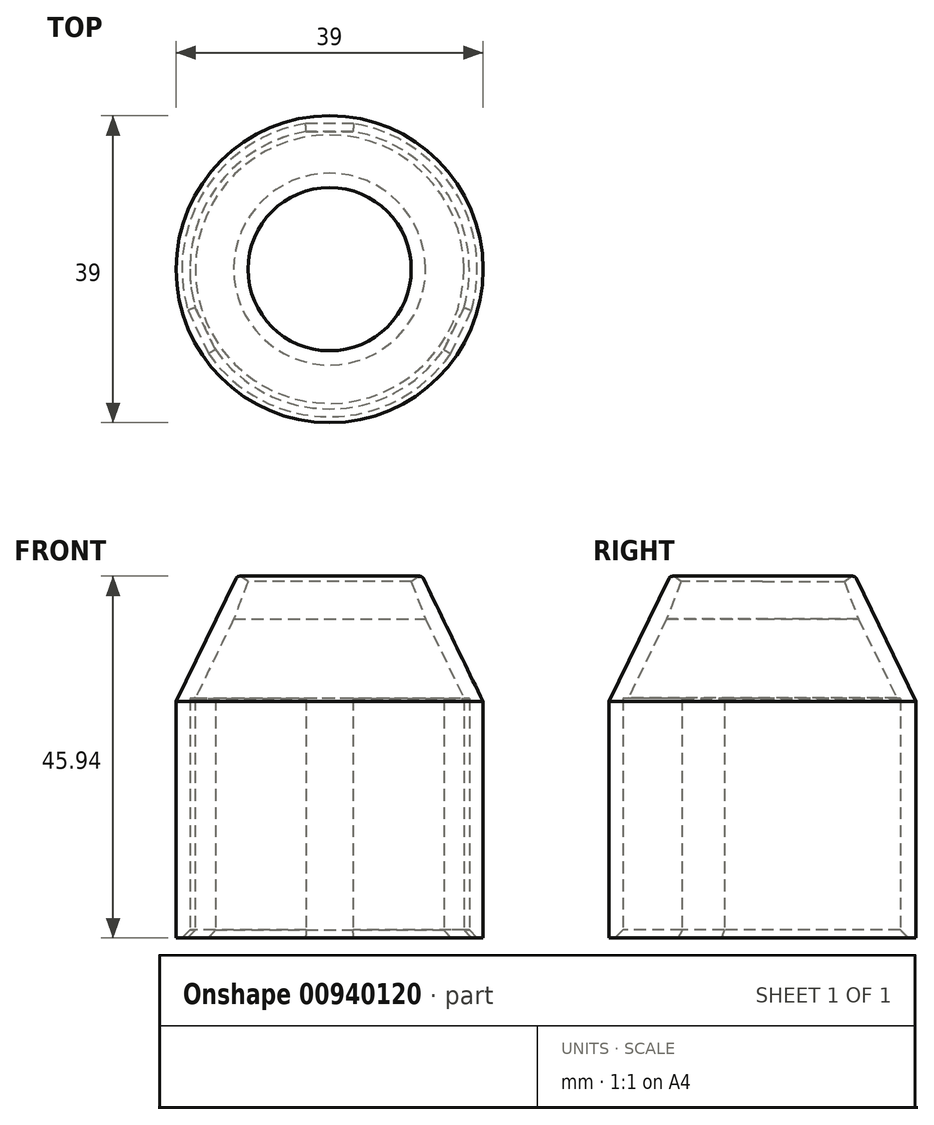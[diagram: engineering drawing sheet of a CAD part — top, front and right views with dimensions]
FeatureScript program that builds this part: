
annotation { "Feature Type Name" : "Feature", "Feature Type Description" : "" }
export const myFeature = defineFeature(function(context is Context, id is Id, definition is map)
    precondition{}
    {
        {
            var Q0;
            Q0=qCreatedBy(makeId("Top.planeOp"),FACE);
            var sketch = newSketch(context, id + "F0", { "sketchPlane" : qUnion([Q0])});
            skCircle(sketch, "E0", {"center": v(0, 0) * mm, "radius": 19.5 * mm});
            skArc(sketch, "E1", {"start": v(-2.97, 17.5) * mm, "mid": v(-15.01, 9.47) * mm, "end": v(-17.07, -4.86) * mm});
            skLineSegment(sketch, "E2", {"start": v(-2.97, 17.5) * mm, "end": v(2.97, 17.5) * mm});
            skLineSegment(sketch, "E3", {"start": v(0, 0) * mm, "end": v(-20.51, -11.84) * mm, "construction": true});
            skLineSegment(sketch, "E4", {"start": v(-17.07, -4.86) * mm, "end": v(-14.51, -10.22) * mm});
            skArc(sketch, "E5.trimOffspring", {"start": v(-14.51, -10.22) * mm, "mid": v(0, -17.75) * mm, "end": v(14.51, -10.22) * mm});
            skPoint(sketch, "E6.MirrorCS.end.orphan", {"position": v(14.51, -10.22) * mm});
            skPoint(sketch, "E6.MirrorCS.start.orphan", {"position": v(17.07, -4.86) * mm});
            skLineSegment(sketch, "E7", {"start": v(14.51, -10.22) * mm, "end": v(17.07, -4.86) * mm});
            skArc(sketch, "E8.trimOffspring", {"start": v(17.07, -4.86) * mm, "mid": v(15.01, 9.47) * mm, "end": v(2.97, 17.5) * mm});
            skSolve(sketch);
        }
        {
            var Q0;
            Q0=qSketchRegion(id+"F0",true);
            extrude(context, id + "F1", {"entities" : qUnion([Q0]), "depth" : 30 * mm, "offsetDistance" : 25 * mm});
        }
        {
            var Q0;
            Q0=qCreatedBy(makeId("Right.planeOp"),FACE);
            var sketch = newSketch(context, id + "F2", { "sketchPlane" : qUnion([Q0])});
            skLineSegment(sketch, "E9.0", {"start": v(-19.5, 30) * mm, "end": v(-17.28, 30) * mm});
            skLineSegment(sketch, "E10", {"start": v(-10, 45) * mm, "end": v(-17.28, 30) * mm});
            skLineSegment(sketch, "E11", {"start": v(-17.28, 30) * mm, "end": v(-19.5, 30) * mm});
            skLineSegment(sketch, "E12", {"start": v(-10, 45) * mm, "end": v(-11.65, 46.2) * mm});
            skLineSegment(sketch, "E13", {"start": v(-11.65, 46.2) * mm, "end": v(-19.5, 30) * mm});
            skPoint(sketch, "E14.orphan", {"position": v(19.5, 30) * mm});
            skSolve(sketch);
        }
        {
            var Q0;
            Q0 = qSketchRegion(id + "F2", true);
            var Q1;
            Q1=makeQuery(id+"F1.opExtrude","SWEPT_FACE",FACE,{"disambiguationData":[OSD([sQuery(id+"F0.wireOp",EDGE,"E8.trimOffspring")])]});
            revolve(context, id + "F3", {"operationType" : NewBodyOperationType.ADD, "surfaceOperationType" : NewSurfaceOperationType.NEW, "entities" : qUnion([Q0]), "axis" : qUnion([Q1]), "revolveType" : RevolveType.FULL});
        }
        {
            var Q0;
            Q0=makeQuery(id+"F3.opRevolve","SWEPT_EDGE",EDGE,{"disambiguationData":[OSD([sQuery(id+"F2.wireOp",EDGE,"E10"),sQuery(id+"F2.wireOp",EDGE,"E11")])]});
            chamfer(context, id + "F4", {"entities" : qUnion([Q0]), "chamferType" : ChamferType.OFFSET_ANGLE, "width" : 5 * mm, "oppositeDirection" : false, "angle" : 5 * degree, "tangentPropagation" : true});
        }
        {
            var Q0;
            Q0=makeQuery(id+"F3.opRevolve","SWEPT_EDGE",EDGE,{"disambiguationData":[OSD([sQuery(id+"F2.wireOp",EDGE,"E10"),sQuery(id+"F2.wireOp",EDGE,"E12")])]});
            var Q1;
            Q1=makeQuery(id+"F3.opRevolve","SWEPT_EDGE",EDGE,{"disambiguationData":[OSD([sQuery(id+"F2.wireOp",EDGE,"E12"),sQuery(id+"F2.wireOp",EDGE,"E13")])]});
            fillet(context, id + "F5", {"entities" : qUnion([Q0, Q1]), "radius" : 0.5 * mm, "tangentPropagation" : true, "allowEdgeOverflow" : false});
        }
        {
            var Q0;
            Q0=makeQuery(id+"F1.opExtrude","CAP_EDGE",EDGE,{"disambiguationData":[OSD([sQuery(id+"F0.wireOp",EDGE,"E8.trimOffspring")])],"isStart":true});
            var Q1;
            Q1=makeQuery(id+"F1.opExtrude","CAP_EDGE",EDGE,{"disambiguationData":[OSD([sQuery(id+"F0.wireOp",EDGE,"E5.trimOffspring")])],"isStart":true});
            var Q2;
            Q2=makeQuery(id+"F1.opExtrude","CAP_EDGE",EDGE,{"disambiguationData":[OSD([sQuery(id+"F0.wireOp",EDGE,"E7")])],"isStart":true});
            var Q3;
            Q3=makeQuery(id+"F1.opExtrude","CAP_EDGE",EDGE,{"disambiguationData":[OSD([sQuery(id+"F0.wireOp",EDGE,"E1")])],"isStart":true});
            var Q4;
            Q4=makeQuery(id+"F1.opExtrude","CAP_EDGE",EDGE,{"disambiguationData":[OSD([sQuery(id+"F0.wireOp",EDGE,"E4")])],"isStart":true});
            var Q5;
            Q5=makeQuery(id+"F1.opExtrude","CAP_EDGE",EDGE,{"disambiguationData":[OSD([sQuery(id+"F0.wireOp",EDGE,"E2")])],"isStart":true});
            chamfer(context, id + "F6", {"entities" : qUnion([Q0, Q1, Q2, Q3, Q4, Q5]), "width" : 1 * mm, "tangentPropagation" : true});
        }
    });
